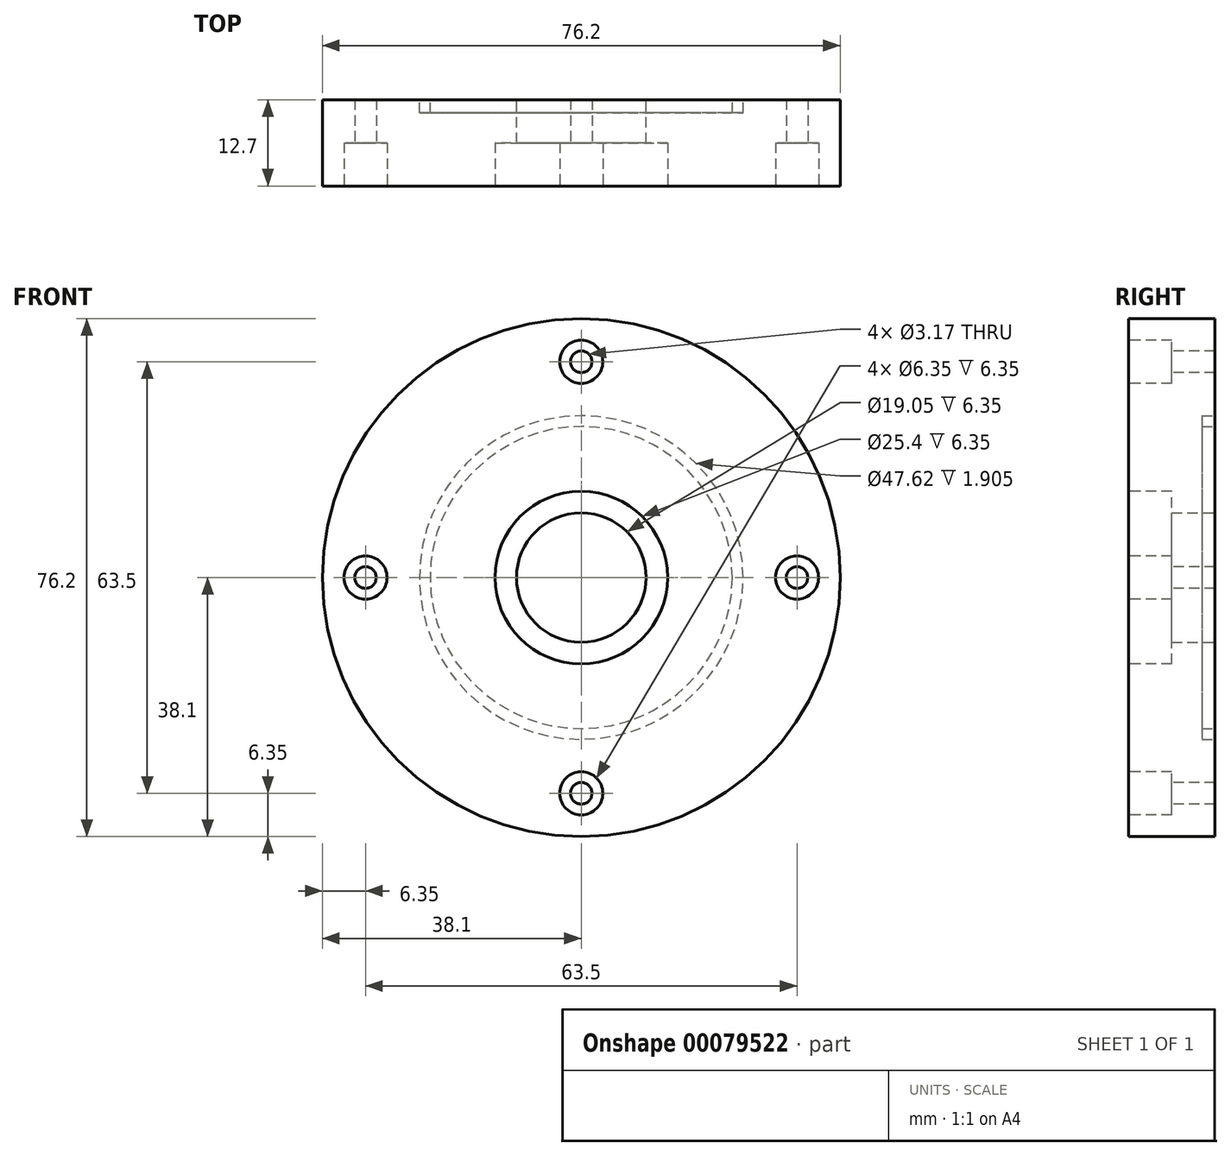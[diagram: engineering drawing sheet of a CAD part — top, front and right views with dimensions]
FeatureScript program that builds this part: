
annotation { "Feature Type Name" : "Feature", "Feature Type Description" : "" }
export const myFeature = defineFeature(function(context is Context, id is Id, definition is map)
    precondition{}
    {
        {
            var Q0;
            Q0=qCreatedBy(makeId("Front.planeOp"),FACE);
            var sketch = newSketch(context, id + "F0", { "sketchPlane" : qUnion([Q0])});
            skCircle(sketch, "E0", {"center": v(0, 0) * mm, "radius": 38.1 * mm});
            skCircle(sketch, "E1", {"center": v(0, 0) * mm, "radius": 9.53 * mm});
            skSolve(sketch);
        }
        {
            var Q0;
            Q0=makeQuery(id+"F0.imprint","IMPRINT",FACE,{"disambiguationData":[TD([[makeQuery(id+"F0.imprint","IMPRINT",EDGE,{"derivedFrom":sQuery(id+"F0.wireOp",EDGE,"E0")}),1.0]])]});
            extrude(context, id + "F1", {"entities" : qUnion([Q0]), "depth" : 12.7 * mm});
        }
        {
            var Q0;
            Q0=makeQuery(id+"F1.opExtrude","CAP_FACE",FACE,{"disambiguationData":[OSD([sQuery(id+"F0.wireOp",EDGE,"E0"),sQuery(id+"F0.wireOp",EDGE,"E1")])],"isStart":false});
            var sketch = newSketch(context, id + "F2", { "sketchPlane" : qUnion([Q0])});
            skCircle(sketch, "E2", {"center": v(0, 0) * mm, "radius": 12.7 * mm});
            skSolve(sketch);
        }
        {
            var Q0;
            Q0=makeQuery(id+"F2.imprint","IMPRINT",FACE,{"disambiguationData":[TD([[makeQuery(id+"F2.imprint","IMPRINT",EDGE,{"derivedFrom":sQuery(id+"F2.wireOp",EDGE,"E2")}),1.0]])]});
            extrude(context, id + "F3", {"entities" : qUnion([Q0]), "operationType" : NewBodyOperationType.REMOVE, "oppositeDirection" : true, "depth" : 6.35 * mm});
        }
        {
            var Q0;
            Q0=makeQuery(id+"F1.opExtrude","CAP_FACE",FACE,{"disambiguationData":[OSD([sQuery(id+"F0.wireOp",EDGE,"E0"),sQuery(id+"F0.wireOp",EDGE,"E1")])],"isStart":false});
            var sketch = newSketch(context, id + "F4", { "sketchPlane" : qUnion([Q0])});
            skPoint(sketch, "E3", {"position": v(0, 31.75) * mm});
            skPoint(sketch, "E4", {"position": v(31.75, 0) * mm});
            skPoint(sketch, "E5", {"position": v(0, -31.75) * mm});
            skPoint(sketch, "E6", {"position": v(-31.75, 0) * mm});
            skSolve(sketch);
        }
        {
            var Q0;
            Q0=sQuery(id+"F4.wireOp",VERTEX,"E3");
            var Q1;
            Q1=sQuery(id+"F4.wireOp",VERTEX,"E4");
            var Q2;
            Q2=sQuery(id+"F4.wireOp",VERTEX,"E5");
            var Q3;
            Q3=sQuery(id+"F4.wireOp",VERTEX,"E6");
            var Q4;
            Q4=makeQuery(id+"F1.opExtrude","SWEPT_BODY",BODY,{"disambiguationData":[OSD([sQuery(id+"F0.wireOp",EDGE,"E0"),sQuery(id+"F0.wireOp",EDGE,"E1")])]});
            hole(context, id + "F5", {"style" : HoleStyle.C_BORE, "endStyle" : HoleEndStyle.THROUGH, "holeDiameter" : 3.17 * mm, "cBoreDiameter" : 6.35 * mm, "cBoreDepth" : 6.35 * mm, "locations" : qUnion([Q0, Q1, Q2, Q3]), "scope" : qUnion([Q4]), "isTappedThrough" : true});
        }
        {
            var Q0;
            Q0=makeQuery(id+"F1.opExtrude","CAP_FACE",FACE,{"disambiguationData":[OSD([sQuery(id+"F0.wireOp",EDGE,"E0"),sQuery(id+"F0.wireOp",EDGE,"E1")])],"isStart":true});
            var sketch = newSketch(context, id + "F6", { "sketchPlane" : qUnion([Q0])});
            skCircle(sketch, "E7", {"center": v(0, 0) * mm, "radius": 23.81 * mm});
            skCircle(sketch, "E8", {"center": v(0, 0) * mm, "radius": 22.23 * mm});
            skSolve(sketch);
        }
        {
            var Q0;
            Q0=makeQuery(id+"F6.imprint","IMPRINT",FACE,{"disambiguationData":[TD([[makeQuery(id+"F6.imprint","IMPRINT",EDGE,{"derivedFrom":sQuery(id+"F6.wireOp",EDGE,"E7")}),1.0]])]});
            extrude(context, id + "F7", {"entities" : qUnion([Q0]), "operationType" : NewBodyOperationType.REMOVE, "oppositeDirection" : true, "depth" : 1.9 * mm});
        }
    });
